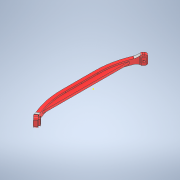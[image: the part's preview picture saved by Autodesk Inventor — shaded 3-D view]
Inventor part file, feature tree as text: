
AUTODESK INVENTOR PART (.ipt)
format: ipt  version: 2022 (Build 260153000, 153)  size: 333,824 bytes
history: native  units: mm
features: sketch x9, extrude x5, plane x3, hole x1, sweep x1, mirror x1, fillet x1
ambient origin geometry x8: Origin, YZ Plane, XZ Plane, XY Plane, X Axis, Y Axis, Z Axis, Center Point
bodies: Solid1 (feature_tree)
feature tree (21):
  extrude  "Extrusion1"  Depth=91.205mm
  extrude  "Extrusion2"  Depth=96.479mm
  extrude  "Extrusion3"  Depth=45.6025mm
  hole  "Hole1"  [1 undecoded]
  plane  "Work Plane1"
  sweep  "Sweep1"
  mirror  "Mirror3"
  plane  "Work Plane3"
  extrude  "Extrusion6"  Depth=2.0mm
  sketch  "Sketch14"  dims[d18=1.0mm]
  fillet  "Fillet2"  Radius=2.0mm
  extrude  "Extrusion8"  Depth=2.0mm
  sketch  "Sketch1"  dims[d0=3.0mm d1=91.205mm]
  sketch  "Sketch2"  dims[d2=3.0mm d3=96.479mm]
  sketch  "Sketch3"  dims[d4=2.301mm d5=45.6025mm]
  sketch  "Sketch4"  dims[d6=48.2395mm d7=0.0mm]
  sketch  "Sketch8"  dims[d8=1.5mm d9=1.5mm]
  sketch  "Sketch9"  dims[d12=6.5mm d13=0.0mm d14=2.0mm d15=2.0mm]
  plane  "Work Plane2"
  sketch  "Sketch11"  dims[d16=2.0mm d17=2.0mm]
  sketch  "Sketch15"  dims[d19=1.0mm d20=1.0mm d21=1.0mm d22=1.0mm d23=1.0mm d24=1.0mm d25=1.0mm d26=6.5mm d27=0.0mm d28=4.0mm d29=4.0mm d30=4.0mm d31=4.0mm d32=3.0mm d33=0.0mm d34=4.25mm d35=2.0mm d36=6.0mm d37=4.0mm d38=2.0mm d39=90.0deg d40=8.0mm d41=20.594885mm d56=0.0mm d57=0.0mm d58=28.0mm d59=28.0mm d60=2.0mm d61=0.0mm d70=7.0mm d71=10.0mm d72=0.0mm]
note: 1 required parameter value undecoded (feature->parameter linkage not recoverable at this tier; creation-order binding heuristic only, values carry confidence <= 0.55)
